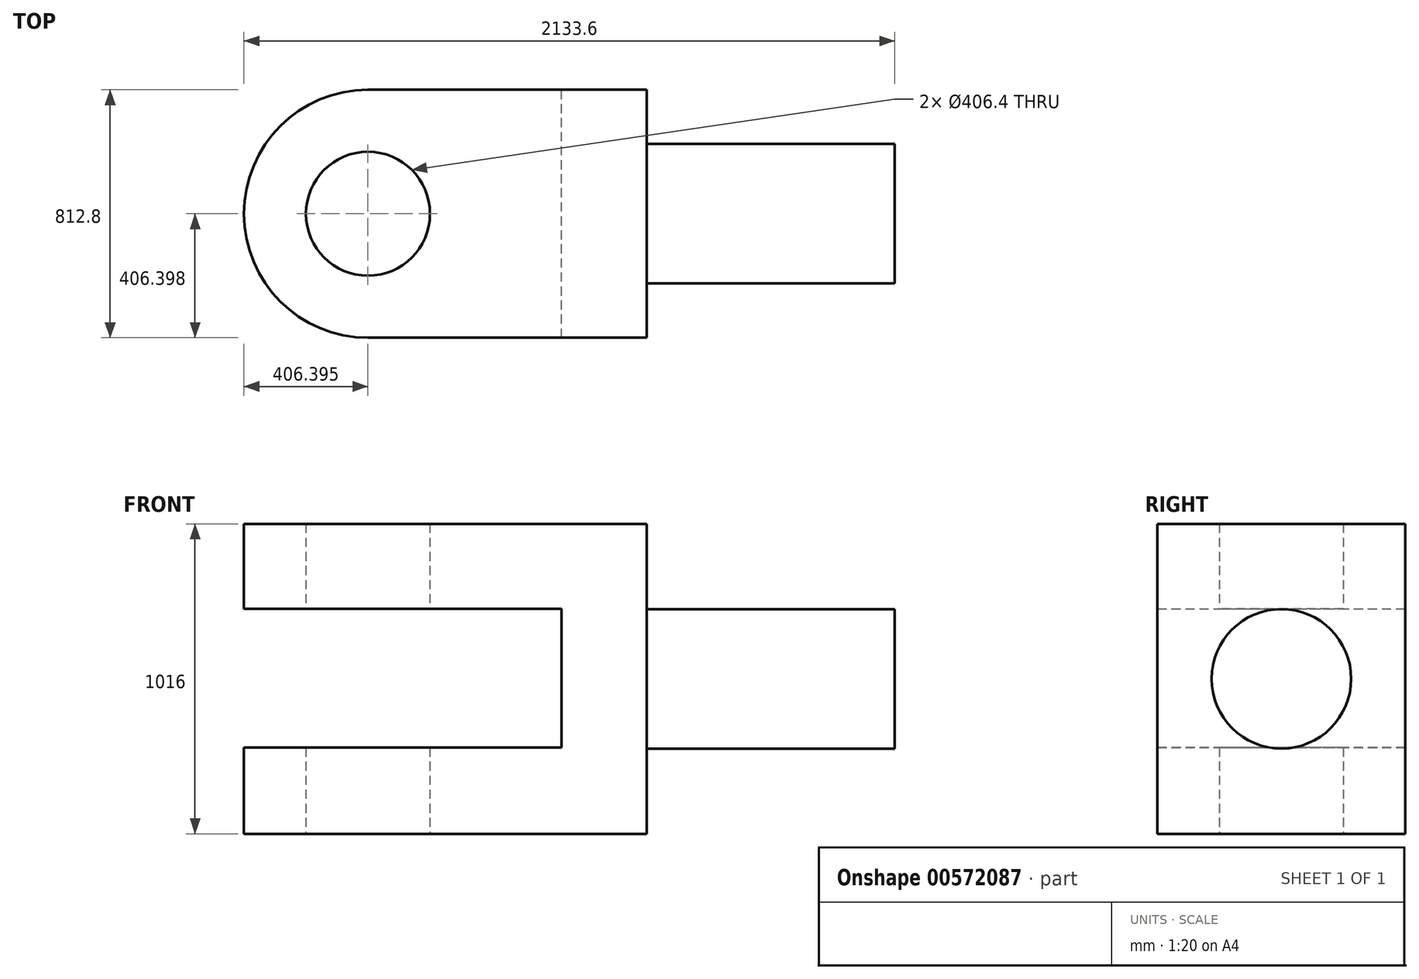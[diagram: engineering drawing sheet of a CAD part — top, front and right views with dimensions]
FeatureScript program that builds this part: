
annotation { "Feature Type Name" : "Feature", "Feature Type Description" : "" }
export const myFeature = defineFeature(function(context is Context, id is Id, definition is map)
    precondition{}
    {
        {
            var Q0;
            Q0=qCreatedBy(makeId("Top.planeOp"),FACE);
            var sketch = newSketch(context, id + "F0", { "sketchPlane" : qUnion([Q0])});
            skLineSegment(sketch, "E0.bottom", {"start": v(-324.96, 298.55) * mm, "end": v(589.44, 298.55) * mm});
            skLineSegment(sketch, "E0.top", {"start": v(-324.96, -514.25) * mm, "end": v(589.44, -514.25) * mm});
            skLineSegment(sketch, "E0.right", {"start": v(589.44, 298.55) * mm, "end": v(589.44, -514.25) * mm});
            skArc(sketch, "E1", {"start": v(-324.96, 298.55) * mm, "mid": v(-731.36, -107.85) * mm, "end": v(-324.96, -514.25) * mm});
            skCircle(sketch, "E2", {"center": v(-324.96, -107.85) * mm, "radius": 203.2 * mm});
            skLineSegment(sketch, "E3", {"start": v(589.44, 298.55) * mm, "end": v(589.44, 120.75) * mm});
            skLineSegment(sketch, "E4", {"start": v(589.44, 120.75) * mm, "end": v(1402.24, 120.75) * mm});
            skLineSegment(sketch, "E5", {"start": v(1402.24, 120.75) * mm, "end": v(1402.24, -336.45) * mm});
            skLineSegment(sketch, "E6", {"start": v(1402.24, -336.45) * mm, "end": v(589.44, -336.45) * mm});
            skLineSegment(sketch, "E7", {"start": v(589.44, -336.45) * mm, "end": v(589.44, -514.25) * mm});
            skSolve(sketch);
        }
        {
            var Q0;
            Q0=makeQuery(id+"F0.imprint","IMPRINT",FACE,{"disambiguationData":[TD([[makeQuery(id+"F0.imprint","IMPRINT",EDGE,{"derivedFrom":sQuery(id+"F0.wireOp",EDGE,"E0.bottom")}),-1.0]])]});
            var Q1;
            Q1=makeQuery(id+"F0.imprint","IMPRINT",FACE,{"disambiguationData":[TD([[makeQuery(id+"F0.imprint","IMPRINT",EDGE,{"derivedFrom":sQuery(id+"F0.wireOp",EDGE,"E0.right")}),1.0]])]});
            extrude(context, id + "F1", {"entities" : qUnion([Q0, Q1]), "depth" : 1016 * mm, "offsetDistance" : 25.4 * mm});
        }
        {
            var Q0;
            Q0=makeQuery(id+"F1.opExtrude","SWEPT_FACE",FACE,{"disambiguationData":[OSD([sQuery(id+"F0.wireOp",EDGE,"E0.bottom")])]});
            var sketch = newSketch(context, id + "F2", { "sketchPlane" : qUnion([Q0])});
            skLineSegment(sketch, "E8", {"start": v(324.96, 0) * mm, "end": v(324.96, 282.6) * mm});
            skLineSegment(sketch, "E9", {"start": v(324.96, 282.6) * mm, "end": v(-309.52, 282.6) * mm});
            skLineSegment(sketch, "E10", {"start": v(-309.52, 282.6) * mm, "end": v(-309.52, 737.25) * mm});
            skLineSegment(sketch, "E11", {"start": v(-309.52, 737.25) * mm, "end": v(324.96, 737.25) * mm});
            skLineSegment(sketch, "E12", {"start": v(324.96, 737.25) * mm, "end": v(324.96, 1016) * mm});
            skLineSegment(sketch, "E13", {"start": v(324.96, 1016) * mm, "end": v(-589.44, 1016) * mm});
            skLineSegment(sketch, "E14", {"start": v(-589.44, 1016) * mm, "end": v(-589.44, 0) * mm});
            skLineSegment(sketch, "E15", {"start": v(-589.44, 0) * mm, "end": v(324.96, 0) * mm});
            skLineSegment(sketch, "E16", {"start": v(324.96, 282.6) * mm, "end": v(324.96, 737.25) * mm});
            skLineSegment(sketch, "E17", {"start": v(324.96, 282.6) * mm, "end": v(821.01, 282.6) * mm});
            skLineSegment(sketch, "E18", {"start": v(324.96, 737.25) * mm, "end": v(892.67, 737.25) * mm});
            skLineSegment(sketch, "E19", {"start": v(892.67, 737.25) * mm, "end": v(821.01, 282.6) * mm});
            skSolve(sketch);
        }
        {
            var Q0;
            Q0=makeQuery(id+"F2.imprint","IMPRINT",FACE,{"disambiguationData":[TD([[makeQuery(id+"F2.imprint","IMPRINT",EDGE,{"derivedFrom":sQuery(id+"F2.wireOp",EDGE,"E9")}),-1.0]])]});
            var Q1;
            Q1=makeQuery(id+"F2.imprint","IMPRINT",FACE,{"disambiguationData":[TD([[makeQuery(id+"F2.imprint","IMPRINT",EDGE,{"derivedFrom":sQuery(id+"F2.wireOp",EDGE,"E16")}),1.0]])]});
            extrude(context, id + "F3", {"entities" : qUnion([Q0, Q1]), "operationType" : NewBodyOperationType.REMOVE, "endBound" : BoundingType.THROUGH_ALL, "oppositeDirection" : true, "depth" : 25.4 * mm, "offsetDistance" : 25.4 * mm});
        }
        {
            var Q0;
            Q0=makeQuery(id+"F1.opExtrude","SWEPT_FACE",FACE,{"disambiguationData":[OSD([sQuery(id+"F0.wireOp",EDGE,"E5")])]});
            var sketch = newSketch(context, id + "F4", { "sketchPlane" : qUnion([Q0])});
            skLineSegment(sketch, "E20", {"start": v(120.75, 1016) * mm, "end": v(120.75, 736.6) * mm});
            skLineSegment(sketch, "E21", {"start": v(120.75, 736.6) * mm, "end": v(-336.45, 736.6) * mm});
            skLineSegment(sketch, "E22", {"start": v(-336.45, 736.6) * mm, "end": v(-336.45, 1016) * mm});
            skLineSegment(sketch, "E23", {"start": v(-336.45, 1016) * mm, "end": v(120.75, 1016) * mm});
            skLineSegment(sketch, "E24", {"start": v(120.75, 0) * mm, "end": v(120.75, 279.4) * mm});
            skLineSegment(sketch, "E25", {"start": v(120.75, 279.4) * mm, "end": v(-336.45, 279.4) * mm});
            skLineSegment(sketch, "E26", {"start": v(-336.45, 279.4) * mm, "end": v(-336.45, 0) * mm});
            skLineSegment(sketch, "E27", {"start": v(-336.45, 0) * mm, "end": v(120.75, 0) * mm});
            skLineSegment(sketch, "E28", {"start": v(-336.45, 736.6) * mm, "end": v(-336.45, 279.4) * mm});
            skSolve(sketch);
        }
        {
            var Q0;
            Q0=makeQuery(id+"F4.imprint","IMPRINT",FACE,{"disambiguationData":[TD([[makeQuery(id+"F4.imprint","IMPRINT",EDGE,{"derivedFrom":sQuery(id+"F4.wireOp",EDGE,"E20")}),-1.0]])]});
            var Q1;
            Q1=makeQuery(id+"F4.imprint","IMPRINT",FACE,{"disambiguationData":[TD([[makeQuery(id+"F4.imprint","IMPRINT",EDGE,{"derivedFrom":sQuery(id+"F4.wireOp",EDGE,"E24")}),-1.0]])]});
            extrude(context, id + "F5", {"entities" : qUnion([Q0, Q1]), "operationType" : NewBodyOperationType.REMOVE, "oppositeDirection" : true, "depth" : 812.8 * mm, "offsetDistance" : 25.4 * mm});
        }
        {
            var Q0;
            Q0=makeQuery(id+"F1.opExtrude","SWEPT_FACE",FACE,{"disambiguationData":[OSD([sQuery(id+"F0.wireOp",EDGE,"E5")])]});
            var sketch = newSketch(context, id + "F6", { "sketchPlane" : qUnion([Q0])});
            skLineSegment(sketch, "E29", {"start": v(-336.45, 279.4) * mm, "end": v(-336.45, 736.6) * mm});
            skCircle(sketch, "E30", {"center": v(-107.85, 508) * mm, "radius": 228.6 * mm});
            skPoint(sketch, "E31.start.orphan", {"position": v(120.75, 736.6) * mm});
            skSolve(sketch);
        }
        {
            var Q0;
            {var subQ0=sQuery(id+"F6.wireOp",EDGE,"E30");var subQ1=makeQuery(id+"F5.boolean.opBoolean","COPY",EDGE,{"derivedFrom":makeQuery(id+"F5.opExtrude","CAP_EDGE",EDGE,{"disambiguationData":[OSD([sQuery(id+"F4.wireOp",EDGE,"E21")])],"isStart":true})});var subQ2=makeQuery(id+"F6.imprint","INTERSECT",VERTEX,{"derivedFrom":[subQ1,subQ0]});Q0=makeQuery(id+"F6.imprint","IMPRINT",FACE,{"disambiguationData":[TD([[makeQuery(id+"F6.imprint","IMPRINT",EDGE,{"disambiguationData":[TD([[subQ2,1.0]])],"derivedFrom":subQ0}),-1.0]])]});}
            var Q1;
            {var subQ0=sQuery(id+"F6.wireOp",EDGE,"E30");var subQ3=makeQuery(id+"F5.boolean.opBoolean","COPY",EDGE,{"derivedFrom":makeQuery(id+"F5.opExtrude","CAP_EDGE",EDGE,{"disambiguationData":[OSD([sQuery(id+"F4.wireOp",EDGE,"E25")])],"isStart":true})});var subQ4=makeQuery(id+"F6.imprint","INTERSECT",VERTEX,{"derivedFrom":[subQ3,subQ0]});Q1=makeQuery(id+"F6.imprint","IMPRINT",FACE,{"disambiguationData":[TD([[makeQuery(id+"F6.imprint","IMPRINT",EDGE,{"disambiguationData":[TD([[subQ4,-1.0]])],"derivedFrom":subQ0}),-1.0]])]});}
            var Q2;
            {var subQ0=sQuery(id+"F6.wireOp",EDGE,"E29");var subQ1=makeQuery(id+"F5.boolean.opBoolean","COPY",EDGE,{"derivedFrom":makeQuery(id+"F5.opExtrude","CAP_EDGE",EDGE,{"disambiguationData":[OSD([sQuery(id+"F4.wireOp",EDGE,"E25")])],"isStart":true})});var subQ2=makeQuery(id+"F6.imprint","INTERSECT",VERTEX,{"derivedFrom":[subQ1,subQ0]});Q2=makeQuery(id+"F6.imprint","IMPRINT",FACE,{"disambiguationData":[TD([[makeQuery(id+"F6.imprint","IMPRINT",EDGE,{"disambiguationData":[TD([[subQ2,1.0]])],"derivedFrom":subQ0}),1.0]])]});}
            var Q3;
            {var subQ0=sQuery(id+"F6.wireOp",EDGE,"E29");var subQ1=makeQuery(id+"F5.boolean.opBoolean","COPY",EDGE,{"derivedFrom":makeQuery(id+"F5.opExtrude","CAP_EDGE",EDGE,{"disambiguationData":[OSD([sQuery(id+"F4.wireOp",EDGE,"E21")])],"isStart":true})});var subQ2=makeQuery(id+"F6.imprint","INTERSECT",VERTEX,{"derivedFrom":[subQ1,subQ0]});Q3=makeQuery(id+"F6.imprint","IMPRINT",FACE,{"disambiguationData":[TD([[makeQuery(id+"F6.imprint","IMPRINT",EDGE,{"disambiguationData":[TD([[subQ2,-1.0]])],"derivedFrom":subQ0}),1.0]])]});}
            extrude(context, id + "F7", {"entities" : qUnion([Q0, Q1, Q2, Q3]), "operationType" : NewBodyOperationType.REMOVE, "oppositeDirection" : true, "depth" : 812.8 * mm, "offsetDistance" : 25.4 * mm});
        }
    });
